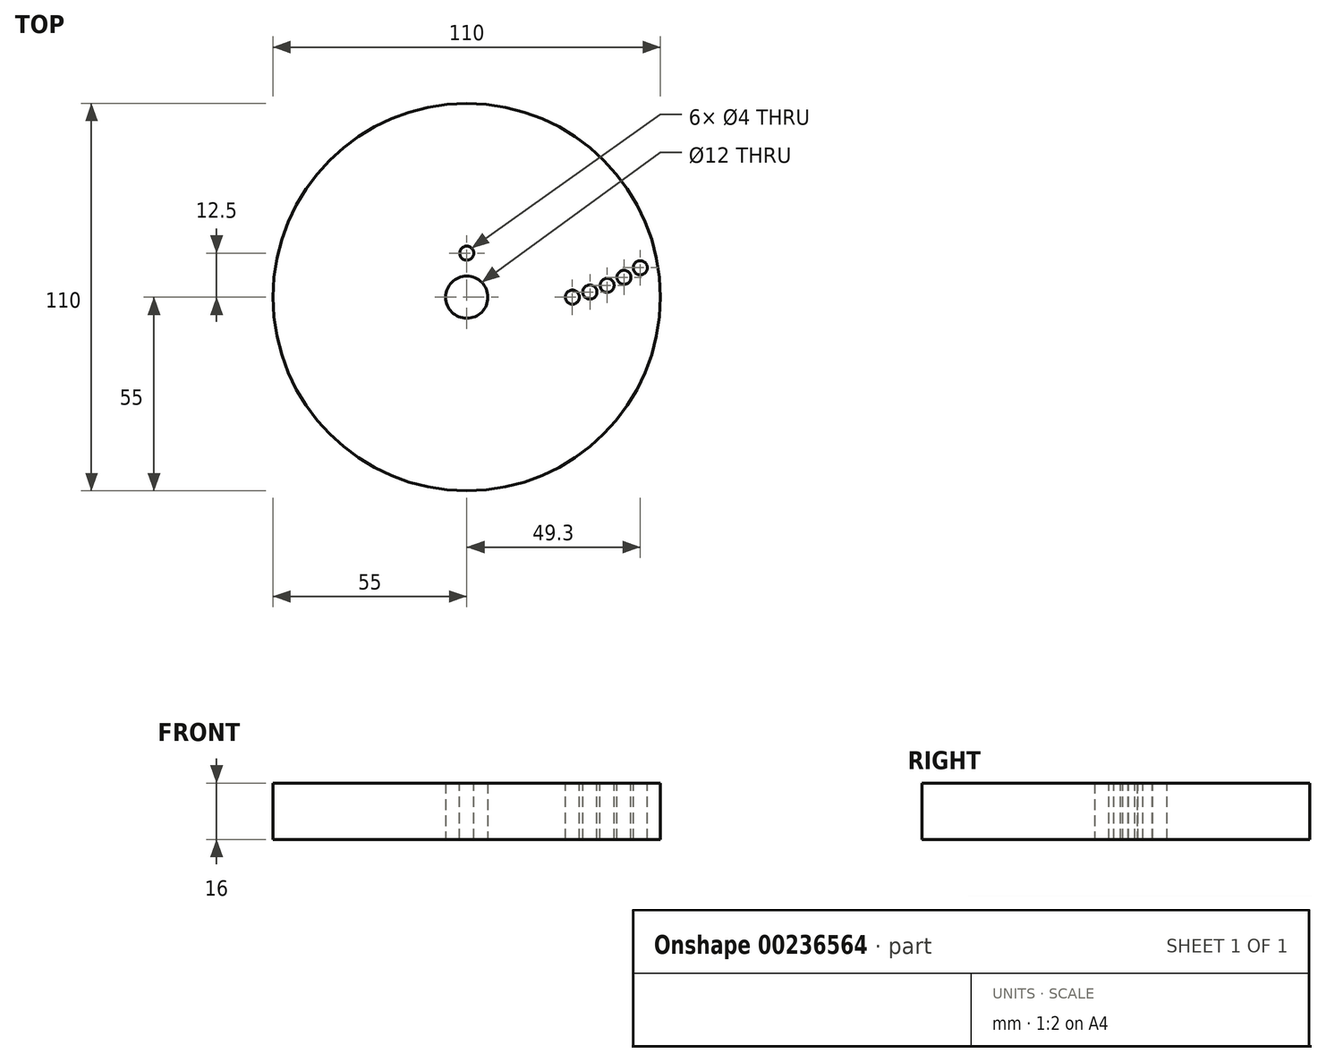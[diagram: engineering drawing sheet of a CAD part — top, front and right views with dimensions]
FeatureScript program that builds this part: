
annotation { "Feature Type Name" : "Feature", "Feature Type Description" : "" }
export const myFeature = defineFeature(function(context is Context, id is Id, definition is map)
    precondition{}
    {
        {
            var Q0;
            Q0=qCreatedBy(makeId("Top.planeOp"),FACE);
            var sketch = newSketch(context, id + "F0", { "sketchPlane" : qUnion([Q0])});
            skCircle(sketch, "E0", {"center": v(0, 0) * mm, "radius": 55 * mm});
            skCircle(sketch, "E1", {"center": v(0, 0) * mm, "radius": 6 * mm});
            skSolve(sketch);
        }
        {
            var Q0;
            Q0 = qSketchRegion(id + "F0", true);
            extrude(context, id + "F1", {"entities" : qUnion([Q0]), "depth" : 16 * mm});
        }
        {
            var Q0;
            Q0=makeQuery(id+"F1.opExtrude","CAP_FACE",FACE,{"disambiguationData":[OSD([sQuery(id+"F0.wireOp",EDGE,"E0"),sQuery(id+"F0.wireOp",EDGE,"E1")])],"isStart":false});
            var sketch = newSketch(context, id + "F2", { "sketchPlane" : qUnion([Q0])});
            skCircle(sketch, "E2", {"center": v(0, 0) * mm, "radius": 30 * mm, "construction": true});
            skCircle(sketch, "E3", {"center": v(0, 0) * mm, "radius": 35 * mm, "construction": true});
            skPoint(sketch, "E4", {"position": v(30, 0) * mm});
            skPoint(sketch, "E5", {"position": v(34.97, 1.47) * mm});
            skPoint(sketch, "E6", {"position": v(39.86, 3.35) * mm});
            skLineSegment(sketch, "E7", {"start": v(39.86, 3.35) * mm, "end": v(0, 0) * mm, "construction": true});
            skLineSegment(sketch, "E8", {"start": v(34.97, 1.47) * mm, "end": v(0, 0) * mm});
            skCircle(sketch, "E9", {"center": v(0, 0) * mm, "radius": 40 * mm, "construction": true});
            skCircle(sketch, "E10", {"center": v(0, 0) * mm, "radius": 45 * mm, "construction": true});
            skCircle(sketch, "E11", {"center": v(0, 0) * mm, "radius": 50 * mm, "construction": true});
            skPoint(sketch, "E12", {"position": v(44.65, 5.64) * mm});
            skPoint(sketch, "E13", {"position": v(49.3, 8.34) * mm});
            skLineSegment(sketch, "E14", {"start": v(44.65, 5.64) * mm, "end": v(0, 0) * mm, "construction": true});
            skLineSegment(sketch, "E15", {"start": v(49.3, 8.34) * mm, "end": v(0, 0) * mm, "construction": true});
            skSolve(sketch);
        }
        {
            var Q0;
            Q0=sQuery(id+"F2.wireOp",VERTEX,"E4");
            var Q1;
            Q1=sQuery(id+"F2.wireOp",VERTEX,"E5");
            var Q2;
            Q2=sQuery(id+"F2.wireOp",VERTEX,"E6");
            var Q3;
            Q3=sQuery(id+"F2.wireOp",VERTEX,"E12");
            var Q4;
            Q4=sQuery(id+"F2.wireOp",VERTEX,"E13");
            var Q5;
            Q5=makeQuery(id+"F1.opExtrude","SWEPT_BODY",BODY,{"disambiguationData":[OSD([sQuery(id+"F0.wireOp",EDGE,"E0"),sQuery(id+"F0.wireOp",EDGE,"E1")])]});
            hole(context, id + "F3", {"style" : HoleStyle.SIMPLE, "endStyle" : HoleEndStyle.THROUGH, "standardTappedOrClearance" : lookupTablePath({ "standard" : "ISO", "size" : "4", "type" : "Drilled" }), "standardBlindInLast" : lookupTablePath({ "standard" : "ISO", "size" : "4", "type" : "Drilled" }), "holeDiameter" : 4 * mm, "locations" : qUnion([Q0, Q1, Q2, Q3, Q4]), "scope" : qUnion([Q5]), "isTappedThrough" : true});
        }
        {
            var Q0;
            Q0=makeQuery(id+"F1.opExtrude","CAP_FACE",FACE,{"disambiguationData":[OSD([sQuery(id+"F0.wireOp",EDGE,"E0"),sQuery(id+"F0.wireOp",EDGE,"E1")])],"isStart":false});
            var sketch = newSketch(context, id + "F4", { "sketchPlane" : qUnion([Q0])});
            skCircle(sketch, "E16", {"center": v(0, 0) * mm, "radius": 12.5 * mm});
            skPoint(sketch, "E17", {"position": v(0, 12.5) * mm});
            skSolve(sketch);
        }
        {
            var Q0;
            Q0=sQuery(id+"F4.wireOp",VERTEX,"E17");
            var Q1;
            Q1=makeQuery(id+"F1.opExtrude","SWEPT_BODY",BODY,{"disambiguationData":[OSD([sQuery(id+"F0.wireOp",EDGE,"E0"),sQuery(id+"F0.wireOp",EDGE,"E1")])]});
            hole(context, id + "F5", {"style" : HoleStyle.SIMPLE, "endStyle" : HoleEndStyle.THROUGH, "standardTappedOrClearance" : lookupTablePath({ "standard" : "ISO", "size" : "4", "type" : "Drilled" }), "standardBlindInLast" : lookupTablePath({ "standard" : "ISO", "size" : "4", "type" : "Drilled" }), "holeDiameter" : 4 * mm, "locations" : qUnion([Q0]), "scope" : qUnion([Q1]), "isTappedThrough" : true});
        }
    });
